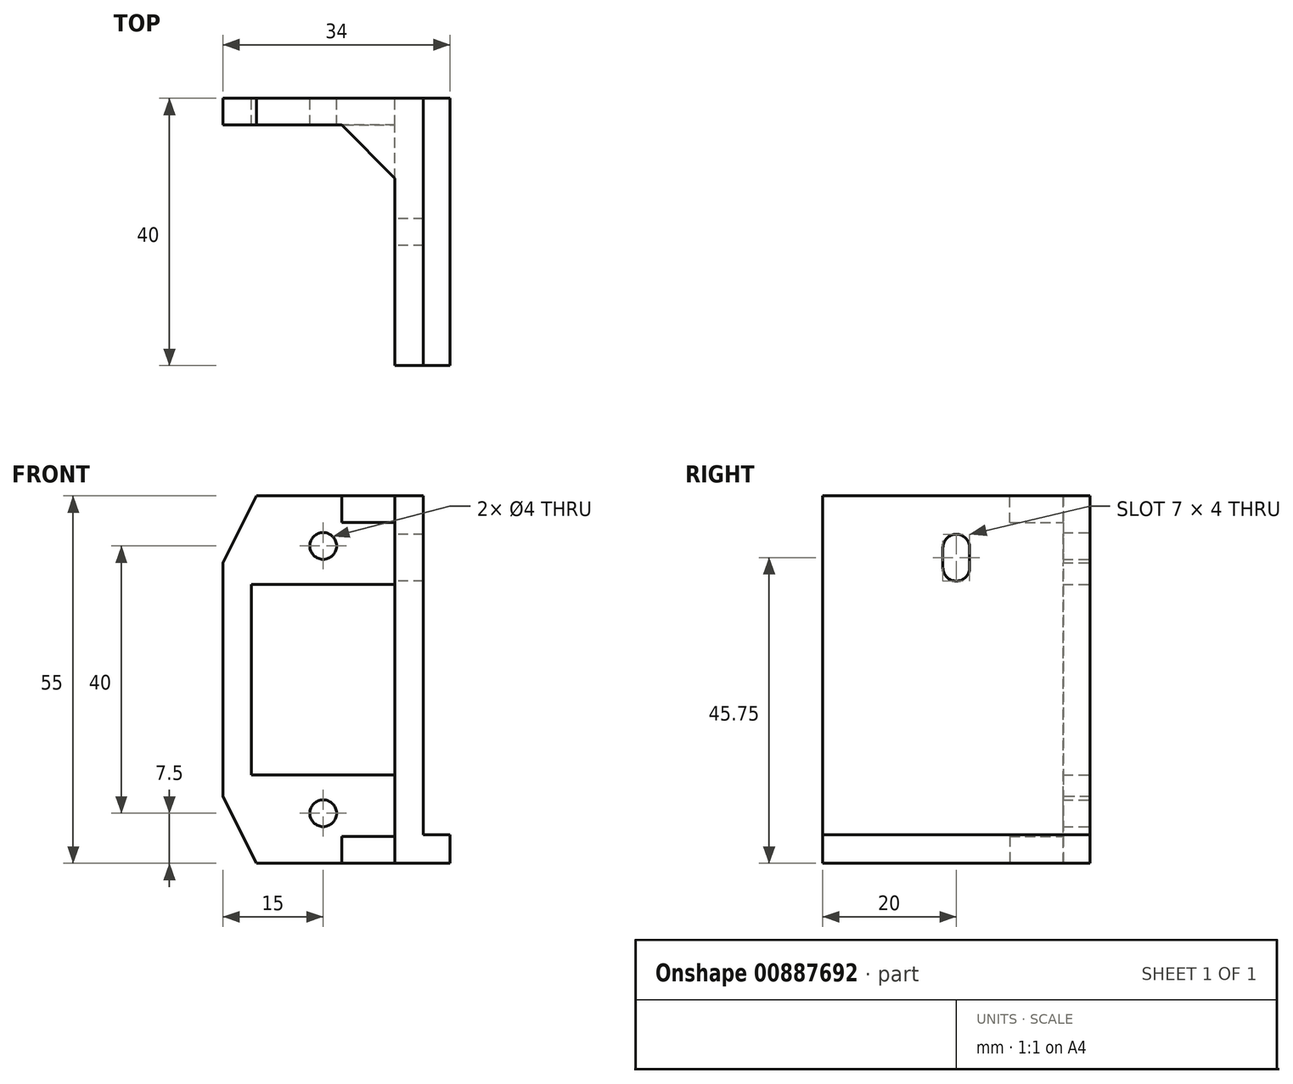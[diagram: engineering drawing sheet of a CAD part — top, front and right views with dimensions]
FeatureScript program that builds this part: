
annotation { "Feature Type Name" : "Feature", "Feature Type Description" : "" }
export const myFeature = defineFeature(function(context is Context, id is Id, definition is map)
    precondition{}
    {
        {
            var Q0;
            Q0=qCreatedBy(makeId("Front.planeOp"),FACE);
            var sketch = newSketch(context, id + "F0", { "sketchPlane" : qUnion([Q0])});
            skLineSegment(sketch, "E0.bottom", {"start": v(0, 0) * mm, "end": v(-30, 0) * mm});
            skLineSegment(sketch, "E0.top", {"start": v(0, 55) * mm, "end": v(-30, 55) * mm});
            skLineSegment(sketch, "E0.left", {"start": v(0, 0) * mm, "end": v(0, 55) * mm});
            skLineSegment(sketch, "E0.right", {"start": v(-30, 0) * mm, "end": v(-30, 55) * mm});
            skLineSegment(sketch, "E1.bottom", {"start": v(-25.75, 41.75) * mm, "end": v(-4.25, 41.75) * mm});
            skLineSegment(sketch, "E1.top", {"start": v(-25.75, 13.25) * mm, "end": v(-4.25, 13.25) * mm});
            skLineSegment(sketch, "E1.left", {"start": v(-25.75, 41.75) * mm, "end": v(-25.75, 13.25) * mm});
            skLineSegment(sketch, "E1.right", {"start": v(-4.25, 41.75) * mm, "end": v(-4.25, 13.25) * mm});
            skPoint(sketch, "E2", {"position": v(-15, 41.75) * mm});
            skPoint(sketch, "E3", {"position": v(-25.75, 27.5) * mm});
            skPoint(sketch, "E4", {"position": v(-15, 55) * mm});
            skPoint(sketch, "E5", {"position": v(-30, 27.5) * mm});
            skCircle(sketch, "E6", {"center": v(-15, 47.5) * mm, "radius": 2 * mm});
            skCircle(sketch, "E7", {"center": v(-15, 7.5) * mm, "radius": 2 * mm});
            skSolve(sketch);
        }
        {
            var Q0;
            Q0=qSketchRegion(id+"F0",true);
            extrude(context, id + "F1", {"entities" : qUnion([Q0]), "depth" : 4 * mm, "offsetDistance" : 25 * mm});
        }
        {
            var Q0;
            Q0=makeQuery(id+"F1.opExtrude","CAP_FACE",FACE,{"disambiguationData":[OSD([sQuery(id+"F0.wireOp",EDGE,"E0.bottom"),sQuery(id+"F0.wireOp",EDGE,"E0.top"),sQuery(id+"F0.wireOp",EDGE,"E0.left"),sQuery(id+"F0.wireOp",EDGE,"E0.right"),sQuery(id+"F0.wireOp",EDGE,"E1.bottom"),sQuery(id+"F0.wireOp",EDGE,"E1.top"),sQuery(id+"F0.wireOp",EDGE,"E1.left"),sQuery(id+"F0.wireOp",EDGE,"E1.right"),sQuery(id+"F0.wireOp",EDGE,"E6"),sQuery(id+"F0.wireOp",EDGE,"E7")])],"isStart":false});
            var sketch = newSketch(context, id + "F2", { "sketchPlane" : qUnion([Q0])});
            skLineSegment(sketch, "E8", {"start": v(0, 55) * mm, "end": v(-4.25, 55) * mm});
            skLineSegment(sketch, "E9", {"start": v(-4.25, 55) * mm, "end": v(-4.25, 0) * mm});
            skLineSegment(sketch, "E10", {"start": v(-4.25, 0) * mm, "end": v(4, 0) * mm});
            skLineSegment(sketch, "E11", {"start": v(4, 0) * mm, "end": v(4, 4.25) * mm});
            skLineSegment(sketch, "E12", {"start": v(4, 4.25) * mm, "end": v(0, 4.25) * mm});
            skLineSegment(sketch, "E13", {"start": v(0, 4.25) * mm, "end": v(0, 55) * mm});
            skSolve(sketch);
        }
        {
            var Q0;
            Q0=qSketchRegion(id+"F2",true);
            extrude(context, id + "F3", {"entities" : qUnion([Q0]), "operationType" : NewBodyOperationType.ADD, "depth" : 36 * mm, "offsetDistance" : 25 * mm});
        }
        {
            var Q0;
            Q0=makeQuery(id+"F3.boolean.opBoolean","MERGE",FACE,{"derivedFrom":[makeQuery(id+"F1.opExtrude","SWEPT_FACE",FACE,{"disambiguationData":[OSD([sQuery(id+"F0.wireOp",EDGE,"E0.top")])]}),makeQuery(id+"F3.opExtrude","SWEPT_FACE",FACE,{"disambiguationData":[OSD([sQuery(id+"F2.wireOp",EDGE,"E8")])]})]});
            var sketch = newSketch(context, id + "F4", { "sketchPlane" : qUnion([Q0])});
            skLineSegment(sketch, "E14", {"start": v(-4.25, -4) * mm, "end": v(-12.25, -4) * mm});
            skLineSegment(sketch, "E15", {"start": v(-12.25, -4) * mm, "end": v(-4.25, -12) * mm});
            skLineSegment(sketch, "E16", {"start": v(-4.25, -12) * mm, "end": v(-4.25, -4) * mm});
            skSolve(sketch);
        }
        {
            var Q0;
            Q0=qSketchRegion(id+"F4",true);
            extrude(context, id + "F5", {"entities" : qUnion([Q0]), "operationType" : NewBodyOperationType.ADD, "oppositeDirection" : true, "depth" : 4 * mm, "offsetDistance" : 25 * mm});
        }
        {
            var Q0;
            Q0=makeQuery(id+"F3.boolean.opBoolean","MERGE",FACE,{"derivedFrom":[makeQuery(id+"F1.opExtrude","SWEPT_FACE",FACE,{"disambiguationData":[OSD([sQuery(id+"F0.wireOp",EDGE,"E1.right")])]}),makeQuery(id+"F3.opExtrude","SWEPT_FACE",FACE,{"disambiguationData":[OSD([sQuery(id+"F2.wireOp",EDGE,"E9")])]})]});
            var sketch = newSketch(context, id + "F6", { "sketchPlane" : qUnion([Q0])});
            skPoint(sketch, "E17.firstSnap0", {"position": v(8, 51) * mm});
            skLineSegment(sketch, "E17.left", {"start": v(18, 47.25) * mm, "end": v(18, 44.25) * mm});
            skLineSegment(sketch, "E17.right", {"start": v(22, 47.25) * mm, "end": v(22, 44.25) * mm});
            skArc(sketch, "E18", {"start": v(22, 47.25) * mm, "mid": v(20, 49.25) * mm, "end": v(18, 47.25) * mm});
            skArc(sketch, "E19", {"start": v(18, 44.25) * mm, "mid": v(20, 42.25) * mm, "end": v(22, 44.25) * mm});
            skSolve(sketch);
        }
        {
            var Q0;
            Q0=makeQuery(id+"F3.opExtrude","CAP_FACE",FACE,{"disambiguationData":[OSD([sQuery(id+"F2.wireOp",EDGE,"E8"),sQuery(id+"F2.wireOp",EDGE,"E9"),sQuery(id+"F2.wireOp",EDGE,"E10"),sQuery(id+"F2.wireOp",EDGE,"E11"),sQuery(id+"F2.wireOp",EDGE,"E12"),sQuery(id+"F2.wireOp",EDGE,"E13")])],"isStart":true});
            var sketch = newSketch(context, id + "F7", { "sketchPlane" : qUnion([Q0])});
            skLineSegment(sketch, "E20.bottom", {"start": v(0, 0) * mm, "end": v(-4, 0) * mm});
            skLineSegment(sketch, "E20.top", {"start": v(0, 4.25) * mm, "end": v(-4, 4.25) * mm});
            skLineSegment(sketch, "E20.left", {"start": v(0, 0) * mm, "end": v(0, 4.25) * mm});
            skLineSegment(sketch, "E20.right", {"start": v(-4, 0) * mm, "end": v(-4, 4.25) * mm});
            skSolve(sketch);
        }
        {
            var Q0;
            Q0=qSketchRegion(id+"F7",true);
            extrude(context, id + "F8", {"entities" : qUnion([Q0]), "operationType" : NewBodyOperationType.ADD, "depth" : 4 * mm, "offsetDistance" : 25 * mm});
        }
        {
            var Q0;
            Q0=makeQuery(id+"F8.boolean.opBoolean","MERGE",FACE,{"derivedFrom":[makeQuery(id+"F3.boolean.opBoolean","MERGE",FACE,{"derivedFrom":[makeQuery(id+"F1.opExtrude","SWEPT_FACE",FACE,{"disambiguationData":[OSD([sQuery(id+"F0.wireOp",EDGE,"E0.bottom")])]}),makeQuery(id+"F3.opExtrude","SWEPT_FACE",FACE,{"disambiguationData":[OSD([sQuery(id+"F2.wireOp",EDGE,"E10")])]})]}),makeQuery(id+"F8.opExtrude","SWEPT_FACE",FACE,{"disambiguationData":[OSD([sQuery(id+"F7.wireOp",EDGE,"E20.bottom")])]})]});
            var sketch = newSketch(context, id + "F9", { "sketchPlane" : qUnion([Q0])});
            skLineSegment(sketch, "E21", {"start": v(-12.25, 4) * mm, "end": v(-4.25, 4) * mm});
            skLineSegment(sketch, "E22", {"start": v(-4.25, 4) * mm, "end": v(-4.25, 12) * mm});
            skLineSegment(sketch, "E23", {"start": v(-4.25, 12) * mm, "end": v(-12.25, 4) * mm});
            skSolve(sketch);
        }
        {
            var Q0;
            Q0=qSketchRegion(id+"F9",true);
            extrude(context, id + "F10", {"entities" : qUnion([Q0]), "operationType" : NewBodyOperationType.ADD, "oppositeDirection" : true, "depth" : 4 * mm, "offsetDistance" : 25 * mm});
        }
        {
            var Q0;
            Q0=qSketchRegion(id+"F6",true);
            extrude(context, id + "F11", {"entities" : qUnion([Q0]), "operationType" : NewBodyOperationType.REMOVE, "endBound" : BoundingType.THROUGH_ALL, "oppositeDirection" : true, "depth" : 25 * mm, "offsetDistance" : 25 * mm});
        }
        {
            var Q0;
            Q0=makeQuery(id+"F1.opExtrude","SWEPT_EDGE",EDGE,{"disambiguationData":[OSD([sQuery(id+"F0.wireOp",EDGE,"E0.bottom"),sQuery(id+"F0.wireOp",EDGE,"E0.right")])]});
            var Q1;
            Q1=makeQuery(id+"F1.opExtrude","SWEPT_EDGE",EDGE,{"disambiguationData":[OSD([sQuery(id+"F0.wireOp",EDGE,"E0.top"),sQuery(id+"F0.wireOp",EDGE,"E0.right")])]});
            chamfer(context, id + "F12", {"entities" : qUnion([Q0, Q1]), "chamferType" : ChamferType.TWO_OFFSETS, "width1" : 5 * mm, "oppositeDirection" : false, "width2" : 10 * mm, "tangentPropagation" : true});
        }
    });
